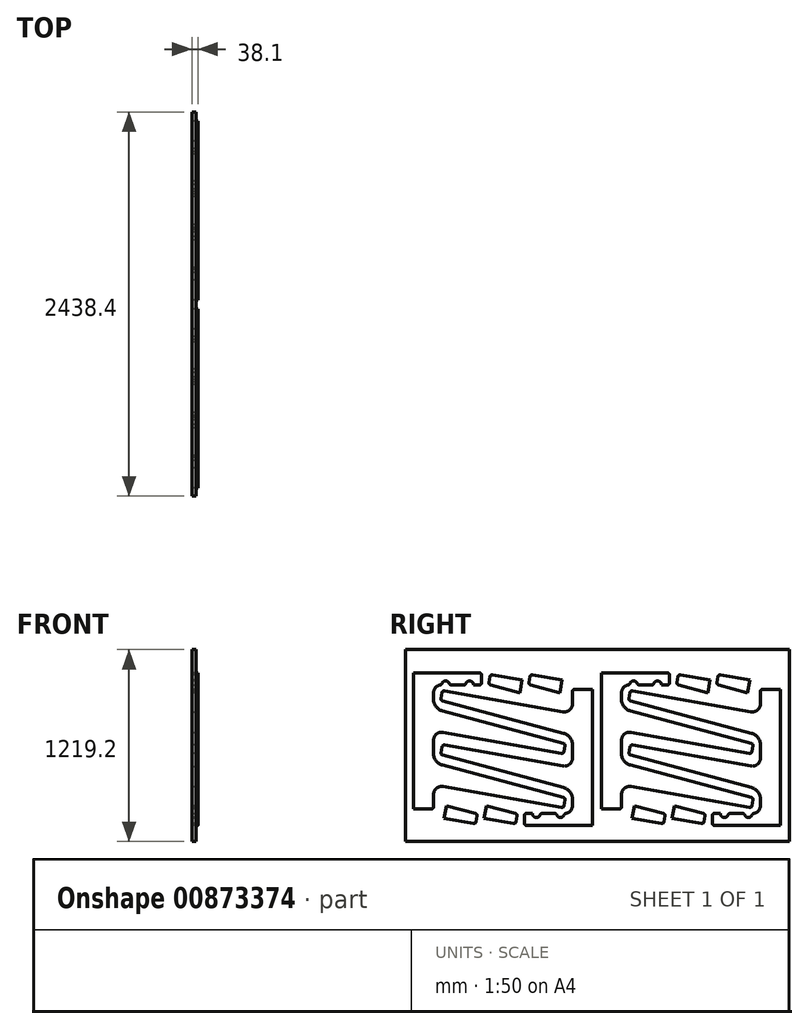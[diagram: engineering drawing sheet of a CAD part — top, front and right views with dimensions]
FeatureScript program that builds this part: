
annotation { "Feature Type Name" : "Feature", "Feature Type Description" : "" }
export const myFeature = defineFeature(function(context is Context, id is Id, definition is map)
    precondition{}
    {
        {
            var Q0;
            Q0=qCreatedBy(makeId("Right.planeOp"),FACE);
            var sketch = newSketch(context, id + "F0", { "sketchPlane" : qUnion([Q0])});
            skLineSegment(sketch, "E0", {"start": v(0, 0) * mm, "end": v(0, 863.6) * mm});
            skLineSegment(sketch, "E1", {"start": v(0, 863.6) * mm, "end": v(-127, 863.6) * mm});
            skLineSegment(sketch, "E2", {"start": v(-127, 863.6) * mm, "end": v(-127, 711.2) * mm});
            skLineSegment(sketch, "E3", {"start": v(-127, 711.2) * mm, "end": v(-952.47, 856.75) * mm});
            skLineSegment(sketch, "E4", {"start": v(-952.47, 856.75) * mm, "end": v(-963.5, 794.22) * mm});
            skLineSegment(sketch, "E5", {"start": v(-963.5, 794.22) * mm, "end": v(-127, 570.08) * mm});
            skLineSegment(sketch, "E6", {"start": v(-127, 570.08) * mm, "end": v(-127, 366.88) * mm});
            skLineSegment(sketch, "E7", {"start": v(-127, 366.88) * mm, "end": v(-952.47, 512.43) * mm});
            skLineSegment(sketch, "E8", {"start": v(-952.47, 512.43) * mm, "end": v(-963.5, 449.9) * mm});
            skLineSegment(sketch, "E9", {"start": v(-963.5, 449.9) * mm, "end": v(-127, 225.76) * mm});
            skLineSegment(sketch, "E10", {"start": v(-127, 225.76) * mm, "end": v(-127, 76.2) * mm});
            skLineSegment(sketch, "E11", {"start": v(-127, 76.2) * mm, "end": v(-431.8, 76.2) * mm});
            skLineSegment(sketch, "E12", {"start": v(-431.8, 76.2) * mm, "end": v(-431.8, 0) * mm});
            skLineSegment(sketch, "E13", {"start": v(-431.8, 0) * mm, "end": v(0, 0) * mm});
            skSolve(sketch);
        }
        {
            var Q0;
            Q0=makeQuery(id+"F0.imprint","IMPRINT",FACE,{"disambiguationData":[TD([[makeQuery(id+"F0.imprint","IMPRINT",EDGE,{"derivedFrom":sQuery(id+"F0.wireOp",EDGE,"E0")}),1.0]])]});
            extrude(context, id + "F1", {"entities" : qUnion([Q0]), "depth" : 38.1 * mm, "offsetDistance" : 25.4 * mm});
        }
        {
            var Q0;
            Q0=makeQuery(id+"F1.opExtrude","SWEPT_EDGE",EDGE,{"disambiguationData":[OSD([sQuery(id+"F0.wireOp",EDGE,"E5"),sQuery(id+"F0.wireOp",EDGE,"E6")])]});
            var Q1;
            Q1=makeQuery(id+"F1.opExtrude","SWEPT_EDGE",EDGE,{"disambiguationData":[OSD([sQuery(id+"F0.wireOp",EDGE,"E9"),sQuery(id+"F0.wireOp",EDGE,"E10")])]});
            fillet(context, id + "F2", {"entities" : qUnion([Q0, Q1]), "radius" : 76.2 * mm, "tangentPropagation" : true, "allowEdgeOverflow" : false});
        }
        {
            var Q0;
            Q0=makeQuery(id+"F1.opExtrude","SWEPT_EDGE",EDGE,{"disambiguationData":[OSD([sQuery(id+"F0.wireOp",EDGE,"E2"),sQuery(id+"F0.wireOp",EDGE,"E3")])]});
            var Q1;
            Q1=makeQuery(id+"F1.opExtrude","SWEPT_EDGE",EDGE,{"disambiguationData":[OSD([sQuery(id+"F0.wireOp",EDGE,"E6"),sQuery(id+"F0.wireOp",EDGE,"E7")])]});
            fillet(context, id + "F3", {"entities" : qUnion([Q0, Q1]), "radius" : 50.8 * mm, "tangentPropagation" : true, "allowEdgeOverflow" : false});
        }
        {
            var Q0;
            Q0=makeQuery(id+"F1.opExtrude","SWEPT_EDGE",EDGE,{"disambiguationData":[OSD([sQuery(id+"F0.wireOp",EDGE,"E3"),sQuery(id+"F0.wireOp",EDGE,"E4")])]});
            var Q1;
            Q1=makeQuery(id+"F1.opExtrude","SWEPT_EDGE",EDGE,{"disambiguationData":[OSD([sQuery(id+"F0.wireOp",EDGE,"E4"),sQuery(id+"F0.wireOp",EDGE,"E5")])]});
            var Q2;
            Q2=makeQuery(id+"F1.opExtrude","SWEPT_EDGE",EDGE,{"disambiguationData":[OSD([sQuery(id+"F0.wireOp",EDGE,"E7"),sQuery(id+"F0.wireOp",EDGE,"E8")])]});
            var Q3;
            Q3=makeQuery(id+"F1.opExtrude","SWEPT_EDGE",EDGE,{"disambiguationData":[OSD([sQuery(id+"F0.wireOp",EDGE,"E8"),sQuery(id+"F0.wireOp",EDGE,"E9")])]});
            var Q4;
            Q4=makeQuery(id+"F1.opExtrude","SWEPT_EDGE",EDGE,{"disambiguationData":[OSD([sQuery(id+"F0.wireOp",EDGE,"E1"),sQuery(id+"F0.wireOp",EDGE,"E2")])]});
            var Q5;
            Q5=makeQuery(id+"F1.opExtrude","SWEPT_EDGE",EDGE,{"disambiguationData":[OSD([sQuery(id+"F0.wireOp",EDGE,"E11"),sQuery(id+"F0.wireOp",EDGE,"E12")])]});
            var Q6;
            Q6=makeQuery(id+"F1.opExtrude","SWEPT_EDGE",EDGE,{"disambiguationData":[OSD([sQuery(id+"F0.wireOp",EDGE,"E12"),sQuery(id+"F0.wireOp",EDGE,"E13")])]});
            fillet(context, id + "F4", {"entities" : qUnion([Q0, Q1, Q2, Q3, Q4, Q5, Q6]), "radius" : 12.7 * mm, "tangentPropagation" : true, "allowEdgeOverflow" : false});
        }
        {
            var Q0;
            Q0=qCreatedBy(makeId("Right.planeOp"),FACE);
            var sketch = newSketch(context, id + "F5", { "sketchPlane" : qUnion([Q0])});
            skLineSegment(sketch, "E14.0", {"start": v(-203.2, 76.2) * mm, "end": v(-419.1, 76.2) * mm, "construction": true});
            skLineSegment(sketch, "E15.0", {"start": v(-431.8, 63.5) * mm, "end": v(-431.8, 12.7) * mm, "construction": true});
            skArc(sketch, "E16", {"start": v(-381, 76.2) * mm, "mid": v(-355.6, 50.8) * mm, "end": v(-330.2, 76.2) * mm});
            skArc(sketch, "E17", {"start": v(-228.6, 76.2) * mm, "mid": v(-203.2, 50.8) * mm, "end": v(-177.8, 76.2) * mm});
            skLineSegment(sketch, "E18", {"start": v(-381, 76.2) * mm, "end": v(-330.2, 76.2) * mm});
            skLineSegment(sketch, "E19", {"start": v(-228.6, 76.2) * mm, "end": v(-177.8, 76.2) * mm});
            skSolve(sketch);
        }
        {
            var Q0;
            Q0=makeQuery(id+"F5.imprint","IMPRINT",FACE,{"disambiguationData":[TD([[makeQuery(id+"F5.imprint","IMPRINT",EDGE,{"derivedFrom":sQuery(id+"F5.wireOp",EDGE,"E16")}),1.0]])]});
            var Q1;
            Q1=makeQuery(id+"F5.imprint","IMPRINT",FACE,{"disambiguationData":[TD([[makeQuery(id+"F5.imprint","IMPRINT",EDGE,{"derivedFrom":sQuery(id+"F5.wireOp",EDGE,"E17")}),1.0]])]});
            extrude(context, id + "F6", {"entities" : qUnion([Q0, Q1]), "operationType" : NewBodyOperationType.REMOVE, "depth" : 76.2 * mm, "offsetDistance" : 25.4 * mm});
        }
        {
            var Q0;
            {var subQ0=sQuery(id+"F5.wireOp",EDGE,"E18");var subQ1=sQuery(id+"F5.wireOp",EDGE,"E16");Q0=makeQuery(id+"F6.boolean.opBoolean","COPY",EDGE,{"derivedFrom":makeQuery(id+"F6.opExtrude","SWEPT_EDGE",EDGE,{"disambiguationData":[OSD([subQ1,subQ0]),TDD([makeQuery(id+"F5.imprint","INTERSECT",VERTEX,{"disambiguationData":[OD(0.0)],"derivedFrom":[subQ1,subQ0]})])]})});}
            var Q1;
            {var subQ0=sQuery(id+"F5.wireOp",EDGE,"E18");var subQ1=sQuery(id+"F5.wireOp",EDGE,"E16");Q1=makeQuery(id+"F6.boolean.opBoolean","COPY",EDGE,{"derivedFrom":makeQuery(id+"F6.opExtrude","SWEPT_EDGE",EDGE,{"disambiguationData":[OSD([subQ1,subQ0]),TDD([makeQuery(id+"F5.imprint","INTERSECT",VERTEX,{"disambiguationData":[OD(1.0)],"derivedFrom":[subQ1,subQ0]})])]})});}
            var Q2;
            {var subQ0=sQuery(id+"F5.wireOp",EDGE,"E19");var subQ1=sQuery(id+"F5.wireOp",EDGE,"E17");Q2=makeQuery(id+"F6.boolean.opBoolean","COPY",EDGE,{"derivedFrom":makeQuery(id+"F6.opExtrude","SWEPT_EDGE",EDGE,{"disambiguationData":[OSD([subQ1,subQ0]),TDD([makeQuery(id+"F5.imprint","INTERSECT",VERTEX,{"disambiguationData":[OD(0.0)],"derivedFrom":[subQ1,subQ0]})])]})});}
            var Q3;
            {var subQ0=sQuery(id+"F5.wireOp",EDGE,"E19");var subQ1=sQuery(id+"F5.wireOp",EDGE,"E17");Q3=makeQuery(id+"F6.boolean.opBoolean","COPY",EDGE,{"derivedFrom":makeQuery(id+"F6.opExtrude","SWEPT_EDGE",EDGE,{"disambiguationData":[OSD([subQ1,subQ0]),TDD([makeQuery(id+"F5.imprint","INTERSECT",VERTEX,{"disambiguationData":[OD(1.0)],"derivedFrom":[subQ1,subQ0]})])]})});}
            fillet(context, id + "F7", {"entities" : qUnion([Q0, Q1, Q2, Q3]), "radius" : 12.7 * mm, "tangentPropagation" : true, "allowEdgeOverflow" : false});
        }
        {
            var Q0;
            Q0=makeQuery(id+"F1.opExtrude","SWEPT_EDGE",EDGE,{"disambiguationData":[OSD([sQuery(id+"F0.wireOp",EDGE,"E10"),sQuery(id+"F0.wireOp",EDGE,"E11")])]});
            fillet(context, id + "F8", {"entities" : qUnion([Q0]), "radius" : 50.8 * mm, "tangentPropagation" : true, "allowEdgeOverflow" : false});
        }
        {
            var Q0;
            Q0=qCreatedBy(makeId("Right.planeOp"),FACE);
            var sketch = newSketch(context, id + "F9", { "sketchPlane" : qUnion([Q0])});
            skLineSegment(sketch, "E20.0", {"start": v(-952.25, 791.2) * mm, "end": v(-766.47, 741.42) * mm});
            skArc(sketch, "E20.1", {"start": v(-961.47, 805.68) * mm, "mid": v(-959.68, 796.65) * mm, "end": v(-952.25, 791.2) * mm});
            skLineSegment(sketch, "E20.2", {"start": v(-954.67, 844.24) * mm, "end": v(-961.47, 805.68) * mm});
            skArc(sketch, "E20.3", {"start": v(-939.96, 854.55) * mm, "mid": v(-949.45, 852.44) * mm, "end": v(-954.67, 844.24) * mm});
            skLineSegment(sketch, "E20.4", {"start": v(-752.35, 821.47) * mm, "end": v(-939.96, 854.55) * mm});
            skLineSegment(sketch, "E21", {"start": v(-766.47, 741.42) * mm, "end": v(-752.35, 821.47) * mm});
            skSolve(sketch);
        }
        {
            var Q0;
            Q0 = qSketchRegion(id + "F9", true);
            extrude(context, id + "F10", {"entities" : qUnion([Q0]), "endBound" : BoundingType.UP_TO_NEXT, "depth" : 25.4 * mm, "offsetDistance" : 25.4 * mm});
        }
        {
            var Q0;
            Q0=makeQuery(id+"F10.opExtrude","SWEPT_BODY",BODY,{"disambiguationData":[OSD([sQuery(id+"F9.wireOp",EDGE,"E20.0"),sQuery(id+"F9.wireOp",EDGE,"E20.1"),sQuery(id+"F9.wireOp",EDGE,"E20.2"),sQuery(id+"F9.wireOp",EDGE,"E20.3"),sQuery(id+"F9.wireOp",EDGE,"E20.4"),sQuery(id+"F9.wireOp",EDGE,"E21")])]});
            transform(context, id + "F11", {"entities" : qUnion([Q0]), "transformType" : TransformType.TRANSLATION_3D, "dx" : 0 * mm, "dy" : 304.8 * mm, "dz" : 101.6 * mm, "makeCopy" : false});
        }
        {
            var Q0;
            Q0=makeQuery(id+"F10.opExtrude","SWEPT_BODY",BODY,{"disambiguationData":[OSD([sQuery(id+"F9.wireOp",EDGE,"E20.0"),sQuery(id+"F9.wireOp",EDGE,"E20.1"),sQuery(id+"F9.wireOp",EDGE,"E20.2"),sQuery(id+"F9.wireOp",EDGE,"E20.3"),sQuery(id+"F9.wireOp",EDGE,"E20.4"),sQuery(id+"F9.wireOp",EDGE,"E21")])]});
            transform(context, id + "F12", {"entities" : qUnion([Q0]), "transformType" : TransformType.TRANSLATION_3D, "dx" : 0 * mm, "dy" : 254 * mm, "dz" : 0 * mm, "makeCopy" : true});
        }
        {
            var Q0;
            Q0=makeQuery(id+"F1.opExtrude","SWEPT_BODY",BODY,{"disambiguationData":[OSD([sQuery(id+"F0.wireOp",EDGE,"E0"),sQuery(id+"F0.wireOp",EDGE,"E1"),sQuery(id+"F0.wireOp",EDGE,"E2"),sQuery(id+"F0.wireOp",EDGE,"E3"),sQuery(id+"F0.wireOp",EDGE,"E4"),sQuery(id+"F0.wireOp",EDGE,"E5"),sQuery(id+"F0.wireOp",EDGE,"E6"),sQuery(id+"F0.wireOp",EDGE,"E7"),sQuery(id+"F0.wireOp",EDGE,"E8"),sQuery(id+"F0.wireOp",EDGE,"E9"),sQuery(id+"F0.wireOp",EDGE,"E10"),sQuery(id+"F0.wireOp",EDGE,"E11"),sQuery(id+"F0.wireOp",EDGE,"E12"),sQuery(id+"F0.wireOp",EDGE,"E13")])]});
            var Q1;
            Q1=makeQuery(id+"F10.opExtrude","SWEPT_BODY",BODY,{"disambiguationData":[OSD([sQuery(id+"F9.wireOp",EDGE,"E20.0"),sQuery(id+"F9.wireOp",EDGE,"E20.1"),sQuery(id+"F9.wireOp",EDGE,"E20.2"),sQuery(id+"F9.wireOp",EDGE,"E20.3"),sQuery(id+"F9.wireOp",EDGE,"E20.4"),sQuery(id+"F9.wireOp",EDGE,"E21")])]});
            var Q2;
            Q2=makeQuery(id+"F12.opPattern","COPY",BODY,{"derivedFrom":makeQuery(id+"F10.opExtrude","SWEPT_BODY",BODY,{"disambiguationData":[OSD([sQuery(id+"F9.wireOp",EDGE,"E20.0"),sQuery(id+"F9.wireOp",EDGE,"E20.1"),sQuery(id+"F9.wireOp",EDGE,"E20.2"),sQuery(id+"F9.wireOp",EDGE,"E20.3"),sQuery(id+"F9.wireOp",EDGE,"E20.4"),sQuery(id+"F9.wireOp",EDGE,"E21")])]}),"instanceName":"1"});
            var Q3;
            Q3=makeQuery(id+"F1.opExtrude","SWEPT_EDGE",EDGE,{"disambiguationData":[OSD([sQuery(id+"F0.wireOp",EDGE,"E0"),sQuery(id+"F0.wireOp",EDGE,"E13")])]});
            transform(context, id + "F13", {"entities" : qUnion([Q0, Q1, Q2]), "transformType" : TransformType.ROTATION, "transformAxis" : qUnion([Q3]), "angle" : 180 * degree, "makeCopy" : true});
        }
        {
            var Q0;
            Q0=makeQuery(id+"F13.opPattern","COPY",BODY,{"derivedFrom":makeQuery(id+"F12.opPattern","COPY",BODY,{"derivedFrom":makeQuery(id+"F10.opExtrude","SWEPT_BODY",BODY,{"disambiguationData":[OSD([sQuery(id+"F9.wireOp",EDGE,"E20.0"),sQuery(id+"F9.wireOp",EDGE,"E20.1"),sQuery(id+"F9.wireOp",EDGE,"E20.2"),sQuery(id+"F9.wireOp",EDGE,"E20.3"),sQuery(id+"F9.wireOp",EDGE,"E20.4"),sQuery(id+"F9.wireOp",EDGE,"E21")])]}),"instanceName":"1"}),"instanceName":"1"});
            var Q1;
            Q1=makeQuery(id+"F13.opPattern","COPY",BODY,{"derivedFrom":makeQuery(id+"F10.opExtrude","SWEPT_BODY",BODY,{"disambiguationData":[OSD([sQuery(id+"F9.wireOp",EDGE,"E20.0"),sQuery(id+"F9.wireOp",EDGE,"E20.1"),sQuery(id+"F9.wireOp",EDGE,"E20.2"),sQuery(id+"F9.wireOp",EDGE,"E20.3"),sQuery(id+"F9.wireOp",EDGE,"E20.4"),sQuery(id+"F9.wireOp",EDGE,"E21")])]}),"instanceName":"1"});
            var Q2;
            Q2=makeQuery(id+"F13.opPattern","COPY",BODY,{"derivedFrom":makeQuery(id+"F1.opExtrude","SWEPT_BODY",BODY,{"disambiguationData":[OSD([sQuery(id+"F0.wireOp",EDGE,"E0"),sQuery(id+"F0.wireOp",EDGE,"E1"),sQuery(id+"F0.wireOp",EDGE,"E2"),sQuery(id+"F0.wireOp",EDGE,"E3"),sQuery(id+"F0.wireOp",EDGE,"E4"),sQuery(id+"F0.wireOp",EDGE,"E5"),sQuery(id+"F0.wireOp",EDGE,"E6"),sQuery(id+"F0.wireOp",EDGE,"E7"),sQuery(id+"F0.wireOp",EDGE,"E8"),sQuery(id+"F0.wireOp",EDGE,"E9"),sQuery(id+"F0.wireOp",EDGE,"E10"),sQuery(id+"F0.wireOp",EDGE,"E11"),sQuery(id+"F0.wireOp",EDGE,"E12"),sQuery(id+"F0.wireOp",EDGE,"E13")])]}),"instanceName":"1"});
            var Q3;
            {var subQ0=sQuery(id+"F0.wireOp",EDGE,"E5");var subQ1=sQuery(id+"F0.wireOp",EDGE,"E4");Q3=makeQuery(id+"F13.opPattern","COPY",VERTEX,{"derivedFrom":makeQuery(id+"F4.opFillet","BLEND_VERTEX",VERTEX,{"blendedFrom":[makeQuery(id+"F1.opExtrude","SWEPT_EDGE",EDGE,{"disambiguationData":[OSD([subQ1,subQ0])]}),makeQuery(id+"F1.opExtrude","SWEPT_FACE",FACE,{"disambiguationData":[OSD([subQ0])]}),makeQuery(id+"F1.opExtrude","CAP_FACE",FACE,{"disambiguationData":[OSD([sQuery(id+"F0.wireOp",EDGE,"E0"),sQuery(id+"F0.wireOp",EDGE,"E1"),sQuery(id+"F0.wireOp",EDGE,"E2"),sQuery(id+"F0.wireOp",EDGE,"E3"),subQ1,subQ0,sQuery(id+"F0.wireOp",EDGE,"E6"),sQuery(id+"F0.wireOp",EDGE,"E7"),sQuery(id+"F0.wireOp",EDGE,"E8"),sQuery(id+"F0.wireOp",EDGE,"E9"),sQuery(id+"F0.wireOp",EDGE,"E10"),sQuery(id+"F0.wireOp",EDGE,"E11"),sQuery(id+"F0.wireOp",EDGE,"E12"),sQuery(id+"F0.wireOp",EDGE,"E13")])],"isStart":true})],"blendedInto":[makeQuery(id+"F1.opExtrude","SWEPT_FACE",FACE,{"disambiguationData":[OSD([subQ0])]}),makeQuery(id+"F1.opExtrude","CAP_FACE",FACE,{"disambiguationData":[OSD([sQuery(id+"F0.wireOp",EDGE,"E0"),sQuery(id+"F0.wireOp",EDGE,"E1"),sQuery(id+"F0.wireOp",EDGE,"E2"),sQuery(id+"F0.wireOp",EDGE,"E3"),subQ1,subQ0,sQuery(id+"F0.wireOp",EDGE,"E6"),sQuery(id+"F0.wireOp",EDGE,"E7"),sQuery(id+"F0.wireOp",EDGE,"E8"),sQuery(id+"F0.wireOp",EDGE,"E9"),sQuery(id+"F0.wireOp",EDGE,"E10"),sQuery(id+"F0.wireOp",EDGE,"E11"),sQuery(id+"F0.wireOp",EDGE,"E12"),sQuery(id+"F0.wireOp",EDGE,"E13")])],"isStart":true})]}),"instanceName":"1"});}
            var Q4;
            {var subQ0=sQuery(id+"F0.wireOp",EDGE,"E9");var subQ1=sQuery(id+"F0.wireOp",EDGE,"E10");Q4=makeQuery(id+"F2.opFillet","BLEND_VERTEX",VERTEX,{"blendedFrom":[makeQuery(id+"F1.opExtrude","SWEPT_EDGE",EDGE,{"disambiguationData":[OSD([subQ0,subQ1])]}),makeQuery(id+"F1.opExtrude","CAP_FACE",FACE,{"disambiguationData":[OSD([sQuery(id+"F0.wireOp",EDGE,"E0"),sQuery(id+"F0.wireOp",EDGE,"E1"),sQuery(id+"F0.wireOp",EDGE,"E2"),sQuery(id+"F0.wireOp",EDGE,"E3"),sQuery(id+"F0.wireOp",EDGE,"E4"),sQuery(id+"F0.wireOp",EDGE,"E5"),sQuery(id+"F0.wireOp",EDGE,"E6"),sQuery(id+"F0.wireOp",EDGE,"E7"),sQuery(id+"F0.wireOp",EDGE,"E8"),subQ0,subQ1,sQuery(id+"F0.wireOp",EDGE,"E11"),sQuery(id+"F0.wireOp",EDGE,"E12"),sQuery(id+"F0.wireOp",EDGE,"E13")])],"isStart":true}),makeQuery(id+"F1.opExtrude","SWEPT_FACE",FACE,{"disambiguationData":[OSD([subQ0])]})],"blendedInto":[makeQuery(id+"F1.opExtrude","CAP_FACE",FACE,{"disambiguationData":[OSD([sQuery(id+"F0.wireOp",EDGE,"E0"),sQuery(id+"F0.wireOp",EDGE,"E1"),sQuery(id+"F0.wireOp",EDGE,"E2"),sQuery(id+"F0.wireOp",EDGE,"E3"),sQuery(id+"F0.wireOp",EDGE,"E4"),sQuery(id+"F0.wireOp",EDGE,"E5"),sQuery(id+"F0.wireOp",EDGE,"E6"),sQuery(id+"F0.wireOp",EDGE,"E7"),sQuery(id+"F0.wireOp",EDGE,"E8"),subQ0,subQ1,sQuery(id+"F0.wireOp",EDGE,"E11"),sQuery(id+"F0.wireOp",EDGE,"E12"),sQuery(id+"F0.wireOp",EDGE,"E13")])],"isStart":true}),makeQuery(id+"F1.opExtrude","SWEPT_FACE",FACE,{"disambiguationData":[OSD([subQ0])]})]});}
            transform(context, id + "F14", {"entities" : qUnion([Q0, Q1, Q2]), "transformType" : TransformType.TRANSLATION_ENTITY, "oppositeDirectionEntity" : false, "transformLine" : qUnion([Q3, Q4]), "makeCopy" : false});
        }
        {
            var Q0;
            Q0=makeQuery(id+"F13.opPattern","COPY",BODY,{"derivedFrom":makeQuery(id+"F1.opExtrude","SWEPT_BODY",BODY,{"disambiguationData":[OSD([sQuery(id+"F0.wireOp",EDGE,"E0"),sQuery(id+"F0.wireOp",EDGE,"E1"),sQuery(id+"F0.wireOp",EDGE,"E2"),sQuery(id+"F0.wireOp",EDGE,"E3"),sQuery(id+"F0.wireOp",EDGE,"E4"),sQuery(id+"F0.wireOp",EDGE,"E5"),sQuery(id+"F0.wireOp",EDGE,"E6"),sQuery(id+"F0.wireOp",EDGE,"E7"),sQuery(id+"F0.wireOp",EDGE,"E8"),sQuery(id+"F0.wireOp",EDGE,"E9"),sQuery(id+"F0.wireOp",EDGE,"E10"),sQuery(id+"F0.wireOp",EDGE,"E11"),sQuery(id+"F0.wireOp",EDGE,"E12"),sQuery(id+"F0.wireOp",EDGE,"E13")])]}),"instanceName":"1"});
            var Q1;
            Q1=makeQuery(id+"F13.opPattern","COPY",BODY,{"derivedFrom":makeQuery(id+"F12.opPattern","COPY",BODY,{"derivedFrom":makeQuery(id+"F10.opExtrude","SWEPT_BODY",BODY,{"disambiguationData":[OSD([sQuery(id+"F9.wireOp",EDGE,"E20.0"),sQuery(id+"F9.wireOp",EDGE,"E20.1"),sQuery(id+"F9.wireOp",EDGE,"E20.2"),sQuery(id+"F9.wireOp",EDGE,"E20.3"),sQuery(id+"F9.wireOp",EDGE,"E20.4"),sQuery(id+"F9.wireOp",EDGE,"E21")])]}),"instanceName":"1"}),"instanceName":"1"});
            var Q2;
            Q2=makeQuery(id+"F13.opPattern","COPY",BODY,{"derivedFrom":makeQuery(id+"F10.opExtrude","SWEPT_BODY",BODY,{"disambiguationData":[OSD([sQuery(id+"F9.wireOp",EDGE,"E20.0"),sQuery(id+"F9.wireOp",EDGE,"E20.1"),sQuery(id+"F9.wireOp",EDGE,"E20.2"),sQuery(id+"F9.wireOp",EDGE,"E20.3"),sQuery(id+"F9.wireOp",EDGE,"E20.4"),sQuery(id+"F9.wireOp",EDGE,"E21")])]}),"instanceName":"1"});
            transform(context, id + "F15", {"entities" : qUnion([Q0, Q1, Q2]), "transformType" : TransformType.TRANSLATION_3D, "dx" : 0 * mm, "dy" : 0 * mm, "dz" : -63.5 * mm, "makeCopy" : false});
        }
        {
            var Q0;
            Q0=makeQuery(id+"F13.opPattern","COPY",BODY,{"derivedFrom":makeQuery(id+"F1.opExtrude","SWEPT_BODY",BODY,{"disambiguationData":[OSD([sQuery(id+"F0.wireOp",EDGE,"E0"),sQuery(id+"F0.wireOp",EDGE,"E1"),sQuery(id+"F0.wireOp",EDGE,"E2"),sQuery(id+"F0.wireOp",EDGE,"E3"),sQuery(id+"F0.wireOp",EDGE,"E4"),sQuery(id+"F0.wireOp",EDGE,"E5"),sQuery(id+"F0.wireOp",EDGE,"E6"),sQuery(id+"F0.wireOp",EDGE,"E7"),sQuery(id+"F0.wireOp",EDGE,"E8"),sQuery(id+"F0.wireOp",EDGE,"E9"),sQuery(id+"F0.wireOp",EDGE,"E10"),sQuery(id+"F0.wireOp",EDGE,"E11"),sQuery(id+"F0.wireOp",EDGE,"E12"),sQuery(id+"F0.wireOp",EDGE,"E13")])]}),"instanceName":"1"});
            var Q1;
            Q1=makeQuery(id+"F1.opExtrude","SWEPT_BODY",BODY,{"disambiguationData":[OSD([sQuery(id+"F0.wireOp",EDGE,"E0"),sQuery(id+"F0.wireOp",EDGE,"E1"),sQuery(id+"F0.wireOp",EDGE,"E2"),sQuery(id+"F0.wireOp",EDGE,"E3"),sQuery(id+"F0.wireOp",EDGE,"E4"),sQuery(id+"F0.wireOp",EDGE,"E5"),sQuery(id+"F0.wireOp",EDGE,"E6"),sQuery(id+"F0.wireOp",EDGE,"E7"),sQuery(id+"F0.wireOp",EDGE,"E8"),sQuery(id+"F0.wireOp",EDGE,"E9"),sQuery(id+"F0.wireOp",EDGE,"E10"),sQuery(id+"F0.wireOp",EDGE,"E11"),sQuery(id+"F0.wireOp",EDGE,"E12"),sQuery(id+"F0.wireOp",EDGE,"E13")])]});
            var Q2;
            Q2=makeQuery(id+"F13.opPattern","COPY",BODY,{"derivedFrom":makeQuery(id+"F12.opPattern","COPY",BODY,{"derivedFrom":makeQuery(id+"F10.opExtrude","SWEPT_BODY",BODY,{"disambiguationData":[OSD([sQuery(id+"F9.wireOp",EDGE,"E20.0"),sQuery(id+"F9.wireOp",EDGE,"E20.1"),sQuery(id+"F9.wireOp",EDGE,"E20.2"),sQuery(id+"F9.wireOp",EDGE,"E20.3"),sQuery(id+"F9.wireOp",EDGE,"E20.4"),sQuery(id+"F9.wireOp",EDGE,"E21")])]}),"instanceName":"1"}),"instanceName":"1"});
            var Q3;
            Q3=makeQuery(id+"F13.opPattern","COPY",BODY,{"derivedFrom":makeQuery(id+"F10.opExtrude","SWEPT_BODY",BODY,{"disambiguationData":[OSD([sQuery(id+"F9.wireOp",EDGE,"E20.0"),sQuery(id+"F9.wireOp",EDGE,"E20.1"),sQuery(id+"F9.wireOp",EDGE,"E20.2"),sQuery(id+"F9.wireOp",EDGE,"E20.3"),sQuery(id+"F9.wireOp",EDGE,"E20.4"),sQuery(id+"F9.wireOp",EDGE,"E21")])]}),"instanceName":"1"});
            var Q4;
            Q4=makeQuery(id+"F10.opExtrude","SWEPT_BODY",BODY,{"disambiguationData":[OSD([sQuery(id+"F9.wireOp",EDGE,"E20.0"),sQuery(id+"F9.wireOp",EDGE,"E20.1"),sQuery(id+"F9.wireOp",EDGE,"E20.2"),sQuery(id+"F9.wireOp",EDGE,"E20.3"),sQuery(id+"F9.wireOp",EDGE,"E20.4"),sQuery(id+"F9.wireOp",EDGE,"E21")])]});
            var Q5;
            Q5=makeQuery(id+"F12.opPattern","COPY",BODY,{"derivedFrom":makeQuery(id+"F10.opExtrude","SWEPT_BODY",BODY,{"disambiguationData":[OSD([sQuery(id+"F9.wireOp",EDGE,"E20.0"),sQuery(id+"F9.wireOp",EDGE,"E20.1"),sQuery(id+"F9.wireOp",EDGE,"E20.2"),sQuery(id+"F9.wireOp",EDGE,"E20.3"),sQuery(id+"F9.wireOp",EDGE,"E20.4"),sQuery(id+"F9.wireOp",EDGE,"E21")])]}),"instanceName":"1"});
            transform(context, id + "F16", {"entities" : qUnion([Q0, Q1, Q2, Q3, Q4, Q5]), "transformType" : TransformType.TRANSLATION_3D, "dx" : 0 * mm, "dy" : 1193.8 * mm, "dz" : 0 * mm, "makeCopy" : true});
        }
        {
            var Q0;
            Q0=qCreatedBy(makeId("Right.planeOp"),FACE);
            var sketch = newSketch(context, id + "F17", { "sketchPlane" : qUnion([Q0])});
            skLineSegment(sketch, "E22.bottom", {"start": v(-1186.53, -101.6) * mm, "end": v(1251.87, -101.6) * mm});
            skLineSegment(sketch, "E22.top", {"start": v(-1186.53, 1117.6) * mm, "end": v(1251.87, 1117.6) * mm});
            skLineSegment(sketch, "E22.left", {"start": v(-1186.53, -101.6) * mm, "end": v(-1186.53, 1117.6) * mm});
            skLineSegment(sketch, "E22.right", {"start": v(1251.87, -101.6) * mm, "end": v(1251.87, 1117.6) * mm});
            skSolve(sketch);
        }
        {
            var Q0;
            Q0=makeQuery(id+"F17.imprint","IMPRINT",FACE,{"disambiguationData":[TD([[makeQuery(id+"F17.imprint","IMPRINT",EDGE,{"derivedFrom":sQuery(id+"F17.wireOp",EDGE,"E22.bottom")}),1.0]])]});
            extrude(context, id + "F18", {"entities" : qUnion([Q0]), "depth" : 25.4 * mm, "offsetDistance" : 25.4 * mm});
        }
    });
